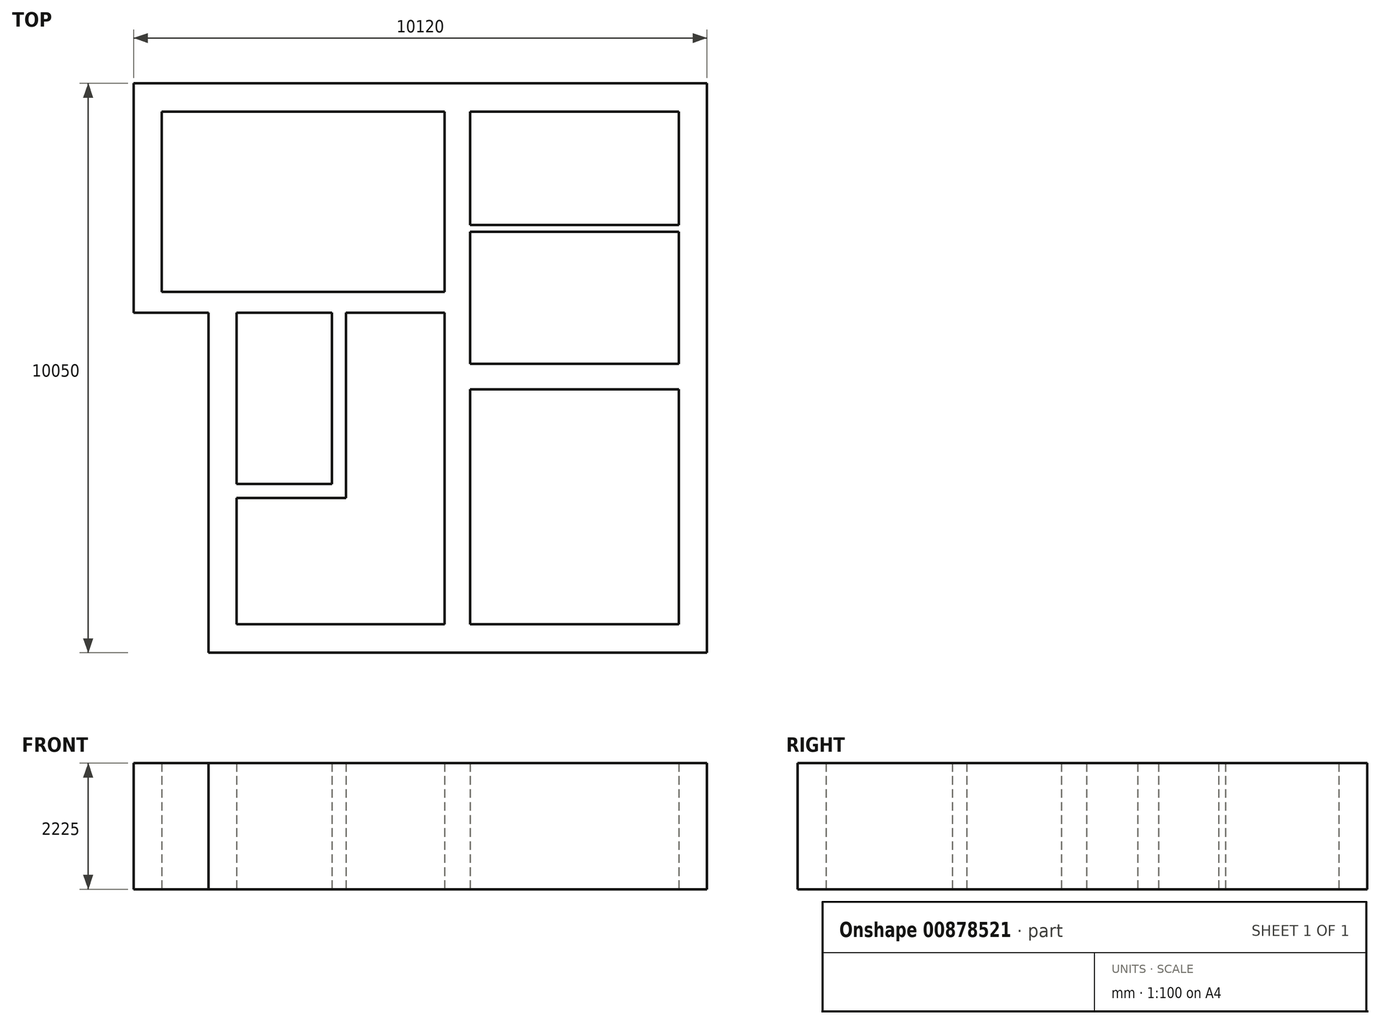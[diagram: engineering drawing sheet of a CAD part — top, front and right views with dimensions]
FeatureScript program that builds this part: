
annotation { "Feature Type Name" : "Feature", "Feature Type Description" : "" }
export const myFeature = defineFeature(function(context is Context, id is Id, definition is map)
    precondition{}
    {
        {
            var Q0;
            Q0=qCreatedBy(makeId("Top.planeOp"),FACE);
            var sketch = newSketch(context, id + "F0", { "sketchPlane" : qUnion([Q0])});
            skLineSegment(sketch, "E0", {"start": v(-6317.16, -9488.66) * mm, "end": v(2482.84, -9488.66) * mm});
            skLineSegment(sketch, "E1", {"start": v(-6317.16, -9488.66) * mm, "end": v(-6317.16, -3488.66) * mm});
            skLineSegment(sketch, "E2", {"start": v(2482.84, -9488.66) * mm, "end": v(2482.84, 561.34) * mm});
            skLineSegment(sketch, "E3", {"start": v(-5817.16, -8988.66) * mm, "end": v(-2147.16, -8988.66) * mm});
            skLineSegment(sketch, "E4", {"start": v(-5817.16, -8988.66) * mm, "end": v(-5817.16, -6758.66) * mm});
            skLineSegment(sketch, "E5", {"start": v(1982.84, 61.34) * mm, "end": v(1982.84, -1938.66) * mm});
            skLineSegment(sketch, "E6", {"start": v(1982.84, 61.34) * mm, "end": v(-1697.16, 61.34) * mm});
            skLineSegment(sketch, "E7", {"start": v(-1697.16, 61.34) * mm, "end": v(-1697.16, -1938.66) * mm});
            skLineSegment(sketch, "E8", {"start": v(-2147.16, 61.34) * mm, "end": v(-2147.16, -8988.66) * mm});
            skLineSegment(sketch, "E9", {"start": v(-2147.16, 61.34) * mm, "end": v(-7137.16, 61.34) * mm});
            skLineSegment(sketch, "E10", {"start": v(-7137.16, 61.34) * mm, "end": v(-7137.16, -3118.66) * mm});
            skLineSegment(sketch, "E11", {"start": v(2482.84, 561.34) * mm, "end": v(-7637.16, 561.34) * mm});
            skLineSegment(sketch, "E12.trimOffspring", {"start": v(-1697.16, -8988.66) * mm, "end": v(1982.84, -8988.66) * mm});
            skLineSegment(sketch, "E13", {"start": v(-7637.16, 561.34) * mm, "end": v(-7637.16, -3488.66) * mm});
            skLineSegment(sketch, "E14", {"start": v(-7637.16, -3488.66) * mm, "end": v(-6317.16, -3488.66) * mm});
            skPoint(sketch, "E15.end.orphan", {"position": v(-7637.16, 61.34) * mm});
            skLineSegment(sketch, "E16", {"start": v(1982.84, -4838.66) * mm, "end": v(-1697.16, -4838.66) * mm});
            skLineSegment(sketch, "E17", {"start": v(-1697.16, -4388.66) * mm, "end": v(1982.84, -4388.66) * mm});
            skLineSegment(sketch, "E18", {"start": v(-5817.16, -3488.66) * mm, "end": v(-4137.16, -3488.66) * mm});
            skLineSegment(sketch, "E19", {"start": v(-4137.16, -3488.66) * mm, "end": v(-4137.16, -6508.66) * mm});
            skLineSegment(sketch, "E20", {"start": v(-3887.16, -6758.66) * mm, "end": v(-3887.16, -3488.66) * mm});
            skLineSegment(sketch, "E21", {"start": v(-3887.16, -6758.66) * mm, "end": v(-5817.16, -6758.66) * mm});
            skLineSegment(sketch, "E22", {"start": v(-4137.16, -6508.66) * mm, "end": v(-5817.16, -6508.66) * mm});
            skLineSegment(sketch, "E23.trimOffspring", {"start": v(-5817.16, -6508.66) * mm, "end": v(-5817.16, -3488.66) * mm});
            skPoint(sketch, "E24.end.orphan", {"position": v(-3887.16, -4463.66) * mm});
            skPoint(sketch, "E24.start.orphan", {"position": v(-2147.16, -4463.66) * mm});
            skLineSegment(sketch, "E25", {"start": v(-7137.16, -3118.66) * mm, "end": v(-2147.16, -3118.66) * mm});
            skLineSegment(sketch, "E26", {"start": v(-3887.16, -3488.66) * mm, "end": v(-2147.16, -3488.66) * mm});
            skLineSegment(sketch, "E27.trimOffspring", {"start": v(-1697.16, -4838.66) * mm, "end": v(-1697.16, -8988.66) * mm});
            skLineSegment(sketch, "E28.trimOffspring", {"start": v(1982.84, -4838.66) * mm, "end": v(1982.84, -8988.66) * mm});
            skLineSegment(sketch, "E29", {"start": v(-1697.16, -2058.66) * mm, "end": v(1982.84, -2058.66) * mm});
            skLineSegment(sketch, "E30", {"start": v(-1697.16, -1938.66) * mm, "end": v(1982.84, -1938.66) * mm});
            skLineSegment(sketch, "E31.trimOffspring", {"start": v(-1697.16, -2058.66) * mm, "end": v(-1697.16, -4388.66) * mm});
            skLineSegment(sketch, "E32.trimOffspring", {"start": v(1982.84, -2058.66) * mm, "end": v(1982.84, -4388.66) * mm});
            skSolve(sketch);
        }
        {
            var Q0;
            Q0 = qSketchRegion(id + "F0", true);
            extrude(context, id + "F1", {"entities" : qUnion([Q0]), "depth" : 2225 * mm, "offsetDistance" : 25 * mm});
        }
    });
